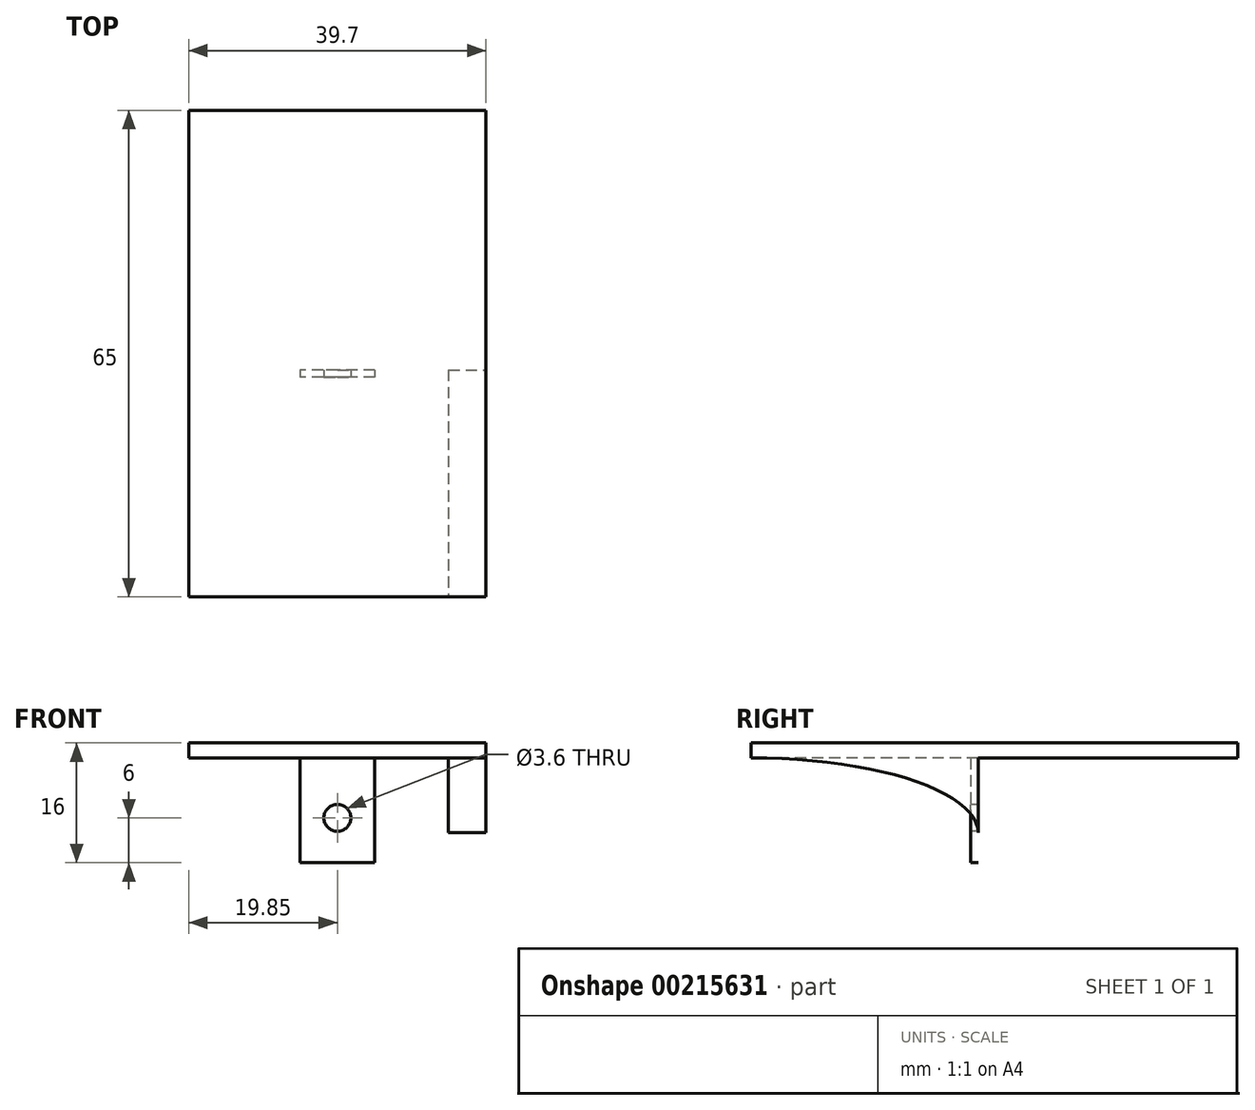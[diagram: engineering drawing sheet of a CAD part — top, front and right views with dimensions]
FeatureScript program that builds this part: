
annotation { "Feature Type Name" : "Feature", "Feature Type Description" : "" }
export const myFeature = defineFeature(function(context is Context, id is Id, definition is map)
    precondition{}
    {
        {
            var Q0;
            Q0=qCreatedBy(makeId("Top.planeOp"),FACE);
            var sketch = newSketch(context, id + "F0", { "sketchPlane" : qUnion([Q0])});
            skLineSegment(sketch, "E0.bottom", {"start": v(19.85, 32.5) * mm, "end": v(-19.85, 32.5) * mm});
            skLineSegment(sketch, "E0.top", {"start": v(19.85, -32.5) * mm, "end": v(-19.85, -32.5) * mm});
            skLineSegment(sketch, "E0.left", {"start": v(19.85, 32.5) * mm, "end": v(19.85, -32.5) * mm});
            skLineSegment(sketch, "E0.right", {"start": v(-19.85, 32.5) * mm, "end": v(-19.85, -32.5) * mm});
            skPoint(sketch, "E0.middle", {"position": v(0, 0) * mm});
            skSolve(sketch);
        }
        {
            var Q0;
            Q0 = qSketchRegion(id + "F0", true);
            extrude(context, id + "F1", {"entities" : qUnion([Q0]), "depth" : 2 * mm});
        }
        {
            var Q0;
            Q0=makeQuery(id+"F1.opExtrude","SWEPT_FACE",FACE,{"disambiguationData":[OSD([sQuery(id+"F0.wireOp",EDGE,"E0.left")])]});
            var sketch = newSketch(context, id + "F2", { "sketchPlane" : qUnion([Q0])});
            skLineSegment(sketch, "E1", {"start": v(-2.16, -10) * mm, "end": v(-2.16, 0) * mm});
            skEllipse(sketch, "E2", {"center": v(-32.5, -10) * mm, "majorRadius": 30.34 * mm, "minorRadius": 10 * mm, "majorAxis": v(1, 0)});
            skSolve(sketch);
        }
        {
            var Q0;
            {var subQ0=sQuery(id+"F2.wireOp",EDGE,"E1");Q0=makeQuery(id+"F2.imprint","IMPRINT",FACE,{"disambiguationData":[TD([[makeQuery(id+"F2.imprint","IMPRINT",EDGE,{"derivedFrom":subQ0}),1.0]])]});}
            extrude(context, id + "F3", {"entities" : qUnion([Q0]), "operationType" : NewBodyOperationType.ADD, "oppositeDirection" : true, "depth" : 5 * mm});
        }
        {
            var Q0;
            Q0=qCreatedBy(makeId("Right.planeOp"),FACE);
            var sketch = newSketch(context, id + "F4", { "sketchPlane" : qUnion([Q0])});
            skLineSegment(sketch, "E3.0", {"start": v(-2.16, -10) * mm, "end": v(-2.16, 0) * mm});
            skLineSegment(sketch, "E4.bottom", {"start": v(-2.16, 0) * mm, "end": v(-3.16, 0) * mm});
            skLineSegment(sketch, "E4.top", {"start": v(-2.16, -14) * mm, "end": v(-3.16, -14) * mm});
            skLineSegment(sketch, "E4.left", {"start": v(-2.16, 0) * mm, "end": v(-2.16, -14) * mm});
            skLineSegment(sketch, "E4.right", {"start": v(-3.16, 0) * mm, "end": v(-3.16, -14) * mm});
            skSolve(sketch);
        }
        {
            var Q0;
            Q0 = qSketchRegion(id + "F4", true);
            extrude(context, id + "F5", {"entities" : qUnion([Q0]), "operationType" : NewBodyOperationType.ADD, "endBound" : BoundingType.SYMMETRIC, "depth" : 10 * mm});
        }
        {
            var Q0;
            Q0=makeQuery(id+"F5.opExtrude","SWEPT_FACE",FACE,{"disambiguationData":[OSD([sQuery(id+"F4.wireOp",EDGE,"E4.right")])]});
            var sketch = newSketch(context, id + "F6", { "sketchPlane" : qUnion([Q0])});
            skCircle(sketch, "E5", {"center": v(0, -8) * mm, "radius": 1.8 * mm});
            skSolve(sketch);
        }
        {
            var Q0;
            Q0 = qSketchRegion(id + "F6", true);
            extrude(context, id + "F7", {"entities" : qUnion([Q0]), "operationType" : NewBodyOperationType.REMOVE, "endBound" : BoundingType.THROUGH_ALL, "oppositeDirection" : true, "depth" : 25 * mm});
        }
    });
